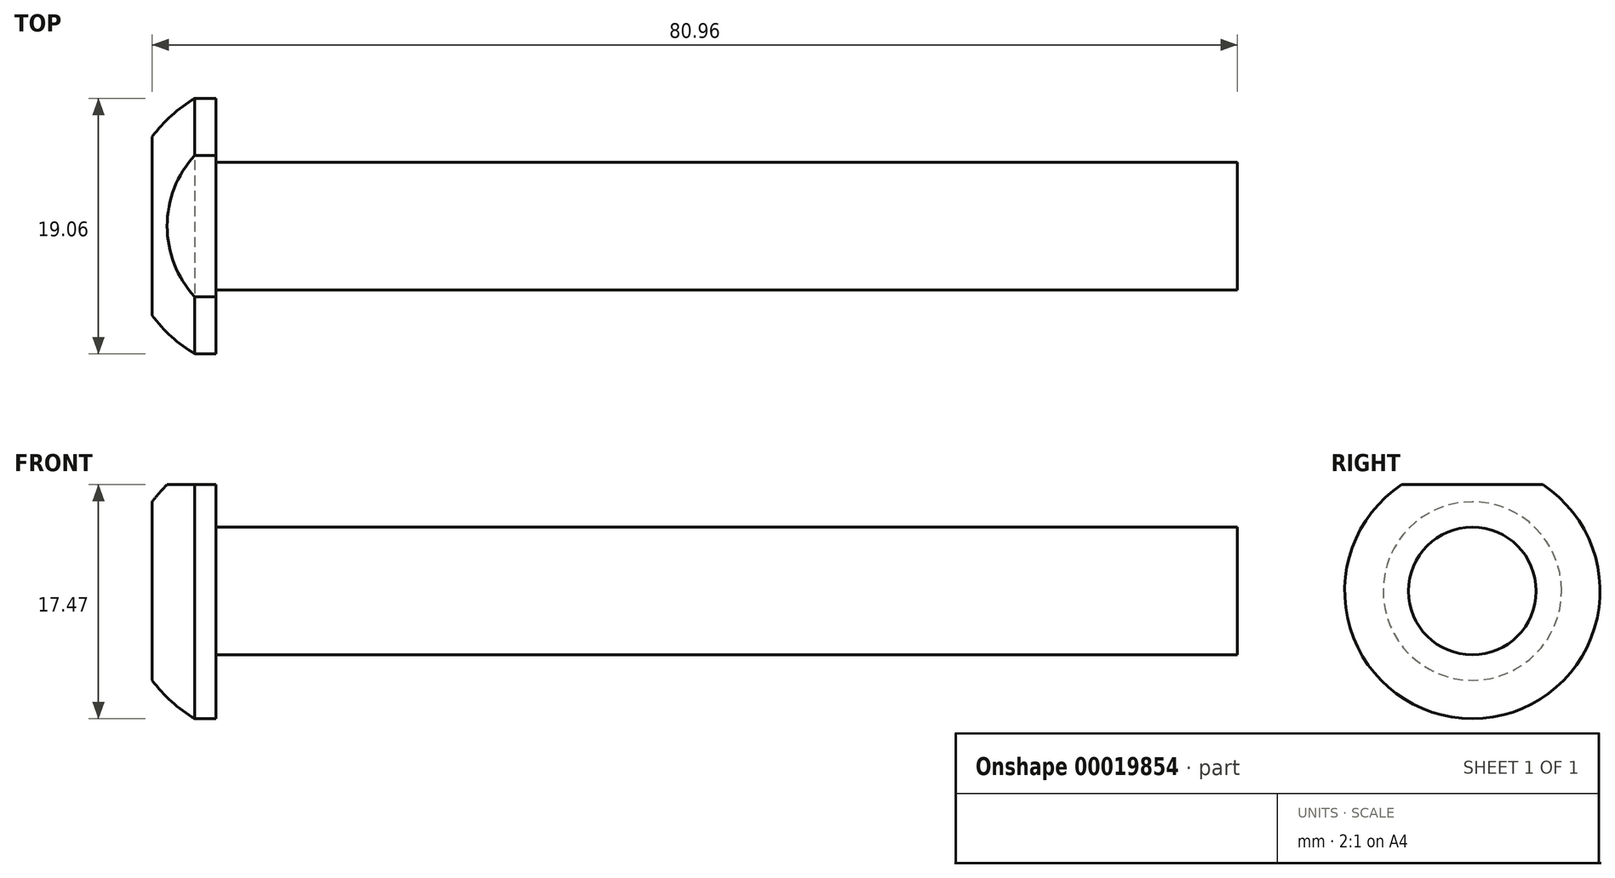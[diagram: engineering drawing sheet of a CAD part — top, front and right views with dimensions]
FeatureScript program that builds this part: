
annotation { "Feature Type Name" : "Feature", "Feature Type Description" : "" }
export const myFeature = defineFeature(function(context is Context, id is Id, definition is map)
    precondition{}
    {
        {
            var Q0;
            Q0=qCreatedBy(makeId("Front.planeOp"),FACE);
            var sketch = newSketch(context, id + "F0", { "sketchPlane" : qUnion([Q0])});
            skLineSegment(sketch, "E0", {"start": v(0, 0) * mm, "end": v(0, 4.76) * mm});
            skLineSegment(sketch, "E1", {"start": v(0, 4.76) * mm, "end": v(-76.2, 4.76) * mm});
            skLineSegment(sketch, "E2", {"start": v(-76.2, 4.76) * mm, "end": v(-76.2, 9.52) * mm});
            skLineSegment(sketch, "E3", {"start": v(-76.2, 9.52) * mm, "end": v(-77.79, 9.52) * mm});
            skLineSegment(sketch, "E4", {"start": v(-80.96, 6.66) * mm, "end": v(-80.96, 0) * mm});
            skLineSegment(sketch, "E5", {"start": v(-80.96, 0) * mm, "end": v(0, 0) * mm});
            skArc(sketch, "E6", {"start": v(-77.79, 9.52) * mm, "mid": v(-79.51, 8.24) * mm, "end": v(-80.96, 6.66) * mm});
            skPoint(sketch, "E7.orphan", {"position": v(-80.96, 9.52) * mm});
            skSolve(sketch);
        }
        {
            var Q0;
            Q0 = qSketchRegion(id + "F0", true);
            var Q1;
            Q1=sQuery(id+"F0.wireOp",EDGE,"E5");
            revolve(context, id + "F1", {"entities" : qUnion([Q0]), "axis" : qUnion([Q1]), "revolveType" : RevolveType.FULL});
        }
        {
            var Q0;
            Q0=makeQuery(id+"F1.opRevolve","SWEPT_FACE",FACE,{"disambiguationData":[OSD([sQuery(id+"F0.wireOp",EDGE,"E4")])]});
            var sketch = newSketch(context, id + "F2", { "sketchPlane" : qUnion([Q0])});
            skLineSegment(sketch, "E8", {"start": v(0, 0) * mm, "end": v(0, 7.94) * mm});
            skLineSegment(sketch, "E9", {"start": v(0, 7.94) * mm, "end": v(-10.94, 7.94) * mm});
            skLineSegment(sketch, "E10", {"start": v(-10.94, 7.94) * mm, "end": v(-10.94, 11.83) * mm});
            skLineSegment(sketch, "E11", {"start": v(-10.94, 11.83) * mm, "end": v(12.12, 11.83) * mm});
            skLineSegment(sketch, "E12", {"start": v(12.12, 11.83) * mm, "end": v(12.12, 7.94) * mm});
            skLineSegment(sketch, "E13", {"start": v(12.12, 7.94) * mm, "end": v(0, 7.94) * mm});
            skSolve(sketch);
        }
        {
            var Q0;
            Q0 = qSketchRegion(id + "F2", true);
            extrude(context, id + "F3", {"entities" : qUnion([Q0]), "operationType" : NewBodyOperationType.REMOVE, "oppositeDirection" : true, "depth" : 25.4 * mm});
        }
    });
